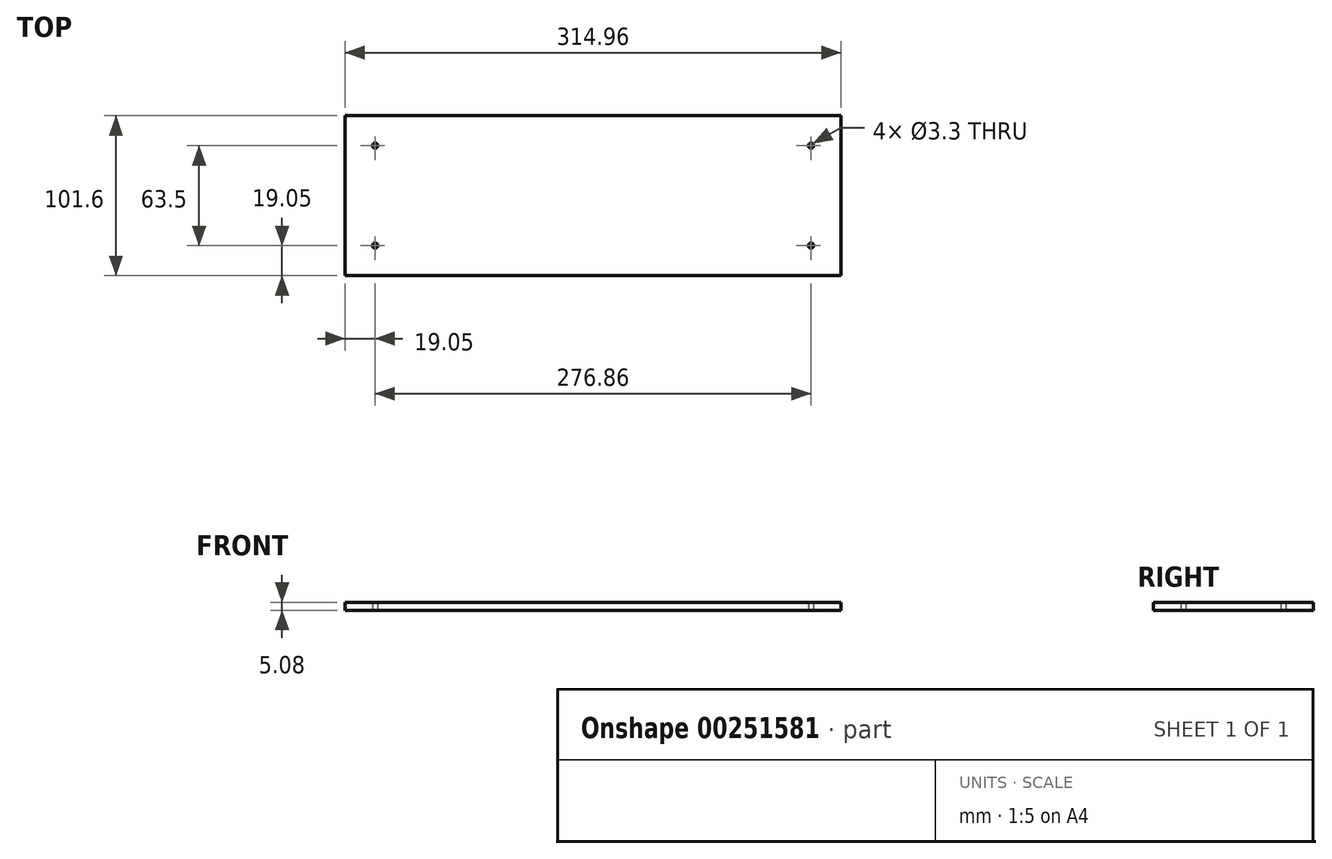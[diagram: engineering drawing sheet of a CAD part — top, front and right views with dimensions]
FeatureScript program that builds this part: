
annotation { "Feature Type Name" : "Feature", "Feature Type Description" : "" }
export const myFeature = defineFeature(function(context is Context, id is Id, definition is map)
    precondition{}
    {
        {
            var Q0;
            Q0=qCreatedBy(makeId("Top.planeOp"),FACE);
            var sketch = newSketch(context, id + "F0", { "sketchPlane" : qUnion([Q0])});
            skLineSegment(sketch, "E0.bottom", {"start": v(-132.08, 50.8) * mm, "end": v(182.88, 50.8) * mm});
            skLineSegment(sketch, "E0.top", {"start": v(-132.08, -50.8) * mm, "end": v(182.88, -50.8) * mm});
            skLineSegment(sketch, "E0.left", {"start": v(-132.08, 50.8) * mm, "end": v(-132.08, -50.8) * mm});
            skLineSegment(sketch, "E0.right", {"start": v(182.88, 50.8) * mm, "end": v(182.88, -50.8) * mm});
            skPoint(sketch, "E1", {"position": v(-113.03, 31.75) * mm});
            skPoint(sketch, "E2", {"position": v(163.83, 31.75) * mm});
            skPoint(sketch, "E3", {"position": v(163.83, -31.75) * mm});
            skPoint(sketch, "E4", {"position": v(-113.03, -31.75) * mm});
            skSolve(sketch);
        }
        {
            var Q0;
            Q0=makeQuery(id+"F0.imprint","IMPRINT",FACE,{"disambiguationData":[TD([[makeQuery(id+"F0.imprint","IMPRINT",EDGE,{"derivedFrom":sQuery(id+"F0.wireOp",EDGE,"E0.bottom")}),-1.0]])]});
            extrude(context, id + "F1", {"entities" : qUnion([Q0]), "depth" : 5.08 * mm});
        }
        {
            var Q0;
            Q0=sQuery(id+"F0.wireOp",VERTEX,"E1");
            var Q1;
            Q1=sQuery(id+"F0.wireOp",VERTEX,"E4");
            var Q2;
            Q2=sQuery(id+"F0.wireOp",VERTEX,"E3");
            var Q3;
            Q3=sQuery(id+"F0.wireOp",VERTEX,"E2");
            var Q4;
            Q4=makeQuery(id+"F1.opExtrude","SWEPT_BODY",BODY,{"disambiguationData":[OSD([sQuery(id+"F0.wireOp",EDGE,"E0.bottom"),sQuery(id+"F0.wireOp",EDGE,"E0.top"),sQuery(id+"F0.wireOp",EDGE,"E0.left"),sQuery(id+"F0.wireOp",EDGE,"E0.right")])]});
            hole(context, id + "F2", {"style" : HoleStyle.SIMPLE, "endStyle" : HoleEndStyle.THROUGH, "oppositeDirection" : true, "holeDiameter" : 3.3 * mm, "tappedDepth" : 12.7 * mm, "tapClearance" : 3, "startFromSketch" : true, "locations" : qUnion([Q0, Q1, Q2, Q3]), "scope" : qUnion([Q4])});
        }
    });
